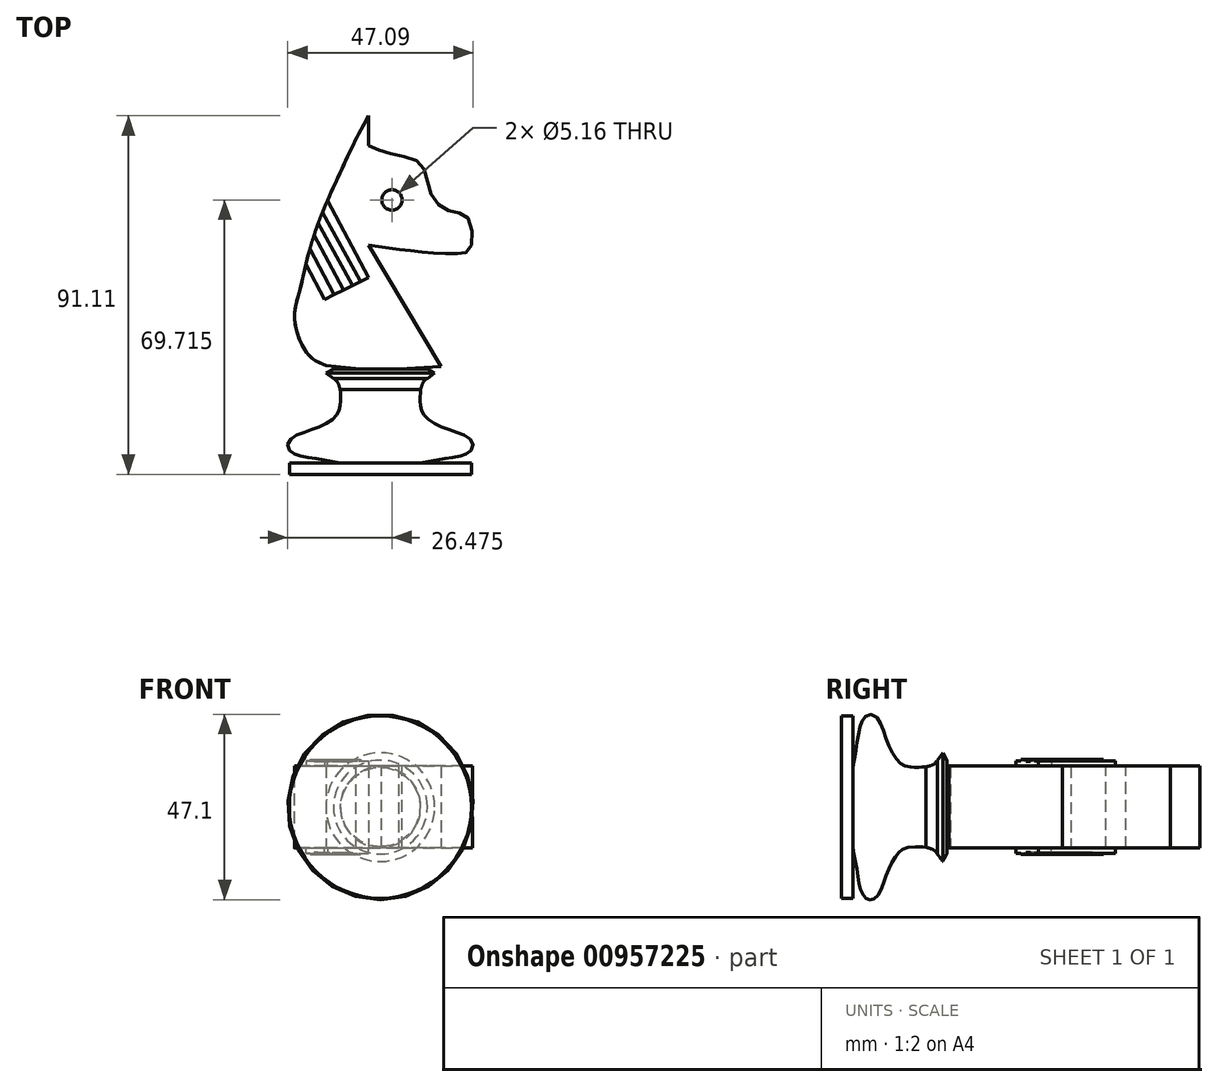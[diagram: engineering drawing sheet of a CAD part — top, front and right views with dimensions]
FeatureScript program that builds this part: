
annotation { "Feature Type Name" : "Feature", "Feature Type Description" : "" }
export const myFeature = defineFeature(function(context is Context, id is Id, definition is map)
    precondition{}
    {
        {
            var Q0;
            Q0=qCreatedBy(makeId("Top.planeOp"),FACE);
            var sketch = newSketch(context, id + "F0", { "sketchPlane" : qUnion([Q0])});
            skLineSegment(sketch, "E0", {"start": v(-38.5, -44.37) * mm, "end": v(-38.5, -41.5) * mm});
            skLineSegment(sketch, "E1", {"start": v(-38.5, -41.5) * mm, "end": v(-25.6, -41.5) * mm});
            skPoint(sketch, "E2.1.internal.snap0", {"position": v(-32.06, -41.5) * mm});
            skPoint(sketch, "E2.5.internal.snap0", {"position": v(-32.06, -41.5) * mm});
            skFitSpline(sketch, "E2", {"points": [v(-25.6, -41.5) * mm, v(-32.06, -40.33) * mm, v(-37.2, -39.16) * mm, v(-38.9, -37.33) * mm, v(-37.85, -35.12) * mm, v(-32.06, -32.77) * mm, v(-27.3, -30.17) * mm, v(-25.6, -27.17) * mm, v(-25.6, -22.87) * mm, v(-25.6, -23) * mm], "startDerivative": vector(-43.27, 8.42) * mm, "endDerivative": vector(0.28, -9.83) * mm});
            skFitSpline(sketch, "E3", {"points": [v(-25.6, -22.87) * mm, v(-26.32, -20.85) * mm, v(-27.3, -20) * mm], "startDerivative": vector(-1, 4.05) * mm, "endDerivative": vector(-2.45, 1.58) * mm});
            skLineSegment(sketch, "E4", {"start": v(-38.5, -44.37) * mm, "end": v(-15.38, -44.37) * mm});
            skLineSegment(sketch, "E5", {"start": v(-15.38, -44.37) * mm, "end": v(-15.38, -17.6) * mm});
            skLineSegment(sketch, "E6", {"start": v(-27.3, -20) * mm, "end": v(-29.19, -18.63) * mm});
            skLineSegment(sketch, "E7", {"start": v(-29.19, -18.63) * mm, "end": v(-27.3, -17.6) * mm});
            skLineSegment(sketch, "E8", {"start": v(-27.3, -17.6) * mm, "end": v(-15.38, -17.6) * mm});
            skPoint(sketch, "E8.endSnap0", {"position": v(-15.38, -14.07) * mm});
            skPoint(sketch, "E9.orphan", {"position": v(-15.38, 16.22) * mm});
            skSolve(sketch);
        }
        {
            var Q0;
            Q0=makeQuery(id+"F0.imprint","IMPRINT",FACE,{"disambiguationData":[TD([[makeQuery(id+"F0.imprint","IMPRINT",EDGE,{"derivedFrom":sQuery(id+"F0.wireOp",EDGE,"E0")}),-1.0]])]});
            var Q1;
            Q1=sQuery(id+"F0.wireOp",EDGE,"E5");
            revolve(context, id + "F1", {"surfaceOperationType" : NewSurfaceOperationType.NEW, "entities" : qUnion([Q0]), "axis" : qUnion([Q1]), "revolveType" : RevolveType.FULL});
        }
        {
            var Q0;
            Q0=qCreatedBy(makeId("Top.planeOp"),FACE);
            var sketch = newSketch(context, id + "F2", { "sketchPlane" : qUnion([Q0])});
            skLineSegment(sketch, "E10", {"start": v(-21.7, -17.55) * mm, "end": v(-29.2, -16.67) * mm});
            skFitSpline(sketch, "E11", {"points": [v(-29.2, -16.67) * mm, v(-31.53, -15.66) * mm, v(-34.24, -13.26) * mm, v(-36.64, -8) * mm, v(-37.18, -3.19) * mm, v(-35.71, 2.93) * mm, v(-34.06, 10.06) * mm, v(-31.1, 19.65) * mm, v(-27.42, 28.3) * mm, v(-22.08, 39.73) * mm, v(-18.4, 46.74) * mm], "startDerivative": vector(-37.65, 13.86) * mm, "endDerivative": vector(32.28, 59.13) * mm});
            skLineSegment(sketch, "E12", {"start": v(-18.4, 46.74) * mm, "end": v(-18.4, 39.18) * mm});
            skFitSpline(sketch, "E13", {"points": [v(-18.4, 39.18) * mm, v(-12.13, 36.97) * mm, v(-4.94, 34.39) * mm, v(-2.73, 27.2) * mm, v(2.06, 22.6) * mm, v(6.86, 20.75) * mm, v(7.45, 13.01) * mm, v(4.5, 11.72) * mm, v(-1.95, 11.9) * mm, v(-8.03, 12.46) * mm, v(-13.56, 13.2) * mm, v(-18.4, 13.93) * mm], "startDerivative": vector(60.8, -26.1) * mm, "endDerivative": vector(-58.19, 9.06) * mm});
            skLineSegment(sketch, "E14", {"start": v(-18.4, 13.93) * mm, "end": v(0, -17.03) * mm});
            skLineSegment(sketch, "E15", {"start": v(0, -17.03) * mm, "end": v(-10.75, -17.59) * mm});
            skLineSegment(sketch, "E16", {"start": v(-10.75, -17.59) * mm, "end": v(-21.7, -17.55) * mm});
            skSolve(sketch);
        }
        {
            var Q0;
            Q0=makeQuery(id+"F2.imprint","IMPRINT",FACE,{"disambiguationData":[TD([[makeQuery(id+"F2.imprint","IMPRINT",EDGE,{"derivedFrom":sQuery(id+"F2.wireOp",EDGE,"E10")}),-1.0]])]});
            extrude(context, id + "F3", {"entities" : qUnion([Q0]), "endBound" : BoundingType.SYMMETRIC, "depth" : 20.83 * mm, "offsetDistance" : 25.4 * mm});
        }
        {
            var Q0;
            Q0=makeQuery(id+"F3.opExtrude","CAP_FACE",FACE,{"disambiguationData":[OSD([sQuery(id+"F2.wireOp",EDGE,"E10"),sQuery(id+"F2.wireOp",EDGE,"E11"),sQuery(id+"F2.wireOp",EDGE,"E12"),sQuery(id+"F2.wireOp",EDGE,"E13"),sQuery(id+"F2.wireOp",EDGE,"E14"),sQuery(id+"F2.wireOp",EDGE,"E15"),sQuery(id+"F2.wireOp",EDGE,"E16")])],"isStart":false});
            var sketch = newSketch(context, id + "F4", { "sketchPlane" : qUnion([Q0])});
            skCircle(sketch, "E17", {"center": v(-12.44, 25.35) * mm, "radius": 2.58 * mm});
            skSolve(sketch);
        }
        {
            var Q0;
            Q0=makeQuery(id+"F4.imprint","IMPRINT",FACE,{"disambiguationData":[TD([[makeQuery(id+"F4.imprint","IMPRINT",EDGE,{"derivedFrom":sQuery(id+"F4.wireOp",EDGE,"E17")}),1.0]])]});
            extrude(context, id + "F5", {"entities" : qUnion([Q0]), "operationType" : NewBodyOperationType.REMOVE, "oppositeDirection" : true, "depth" : 72.9 * mm, "offsetDistance" : 25.4 * mm});
        }
        {
            var Q0;
            Q0=makeQuery(id+"F3.opExtrude","CAP_FACE",FACE,{"disambiguationData":[OSD([sQuery(id+"F2.wireOp",EDGE,"E10"),sQuery(id+"F2.wireOp",EDGE,"E11"),sQuery(id+"F2.wireOp",EDGE,"E12"),sQuery(id+"F2.wireOp",EDGE,"E13"),sQuery(id+"F2.wireOp",EDGE,"E14"),sQuery(id+"F2.wireOp",EDGE,"E15"),sQuery(id+"F2.wireOp",EDGE,"E16")])],"isStart":false});
            var sketch = newSketch(context, id + "F6", { "sketchPlane" : qUnion([Q0])});
            skLineSegment(sketch, "E18", {"start": v(-31.2, 19.42) * mm, "end": v(-22.64, 3.86) * mm});
            skLineSegment(sketch, "E19", {"start": v(-32.22, 16.44) * mm, "end": v(-24.92, 2.7) * mm});
            skLineSegment(sketch, "E20", {"start": v(-30.12, 22.18) * mm, "end": v(-20.58, 4.81) * mm});
            skLineSegment(sketch, "E21", {"start": v(-28.82, 25.2) * mm, "end": v(-18.38, 5.68) * mm});
            skLineSegment(sketch, "E22", {"start": v(-33.3, 12.88) * mm, "end": v(-27.27, 1.52) * mm});
            skLineSegment(sketch, "E23", {"start": v(-34.32, 8.94) * mm, "end": v(-29.57, 0) * mm});
            skLineSegment(sketch, "E24", {"start": v(-29.57, 0) * mm, "end": v(-18.38, 5.68) * mm});
            skLineSegment(sketch, "E25", {"start": v(-27.27, 1.52) * mm, "end": v(-27.11, 1.25) * mm});
            skLineSegment(sketch, "E26", {"start": v(-24.92, 2.7) * mm, "end": v(-24.78, 2.43) * mm});
            skLineSegment(sketch, "E27", {"start": v(-22.64, 3.86) * mm, "end": v(-22.5, 3.59) * mm});
            skLineSegment(sketch, "E28", {"start": v(-20.58, 4.81) * mm, "end": v(-20.48, 4.62) * mm});
            skFitSpline(sketch, "E29", {"points": [v(-28.82, 25.2) * mm, v(-30.12, 22.18) * mm, v(-31.2, 19.42) * mm, v(-32.22, 16.44) * mm, v(-33.3, 12.88) * mm, v(-34.32, 8.94) * mm], "startDerivative": vector(-6.83, -15.64) * mm, "endDerivative": vector(-4.54, -18.23) * mm});
            skSolve(sketch);
        }
        {
            var Q0;
            {var subQ6=sQuery(id+"F6.wireOp",EDGE,"E22");Q0=makeQuery(id+"F6.imprint","IMPRINT",FACE,{"disambiguationData":[TD([[makeQuery(id+"F6.imprint","IMPRINT",EDGE,{"derivedFrom":subQ6}),-1.0]])]});}
            var Q1;
            {var subQ3=sQuery(id+"F6.wireOp",EDGE,"E20");Q1=makeQuery(id+"F6.imprint","IMPRINT",FACE,{"disambiguationData":[TD([[makeQuery(id+"F6.imprint","IMPRINT",EDGE,{"derivedFrom":subQ3}),1.0]])]});}
            extrude(context, id + "F7", {"entities" : qUnion([Q0, Q1]), "operationType" : NewBodyOperationType.ADD, "depth" : 1.35 * mm, "offsetDistance" : 25.4 * mm});
        }
        {
            var Q0;
            {var subQ4=sQuery(id+"F6.wireOp",EDGE,"E19");Q0=makeQuery(id+"F6.imprint","IMPRINT",FACE,{"disambiguationData":[TD([[makeQuery(id+"F6.imprint","IMPRINT",EDGE,{"derivedFrom":subQ4}),-1.0]])]});}
            var Q1;
            {var subQ3=sQuery(id+"F6.wireOp",EDGE,"E18");Q1=makeQuery(id+"F6.imprint","IMPRINT",FACE,{"disambiguationData":[TD([[makeQuery(id+"F6.imprint","IMPRINT",EDGE,{"derivedFrom":subQ3}),1.0]])]});}
            extrude(context, id + "F8", {"entities" : qUnion([Q0, Q1]), "operationType" : NewBodyOperationType.ADD, "depth" : 1.65 * mm, "offsetDistance" : 25.4 * mm});
        }
        {
            var Q0;
            {var subQ4=sQuery(id+"F6.wireOp",EDGE,"E18");Q0=makeQuery(id+"F6.imprint","IMPRINT",FACE,{"disambiguationData":[TD([[makeQuery(id+"F6.imprint","IMPRINT",EDGE,{"derivedFrom":subQ4}),-1.0]])]});}
            extrude(context, id + "F9", {"entities" : qUnion([Q0]), "operationType" : NewBodyOperationType.ADD, "depth" : 1.14 * mm, "offsetDistance" : 25.4 * mm});
        }
        {
            var Q0;
            Q0=makeQuery(id+"F3.opExtrude","SWEPT_BODY",BODY,{"disambiguationData":[OSD([sQuery(id+"F2.wireOp",EDGE,"E10"),sQuery(id+"F2.wireOp",EDGE,"E11"),sQuery(id+"F2.wireOp",EDGE,"E12"),sQuery(id+"F2.wireOp",EDGE,"E13"),sQuery(id+"F2.wireOp",EDGE,"E14"),sQuery(id+"F2.wireOp",EDGE,"E15"),sQuery(id+"F2.wireOp",EDGE,"E16")])]});
            var Q1;
            Q1=qCreatedBy(makeId("Top.planeOp"),FACE);
            mirror(context, id + "F10", {"operationType" : NewBodyOperationType.ADD, "entities" : qUnion([Q0]), "mirrorPlane" : qUnion([Q1])});
        }
    });
